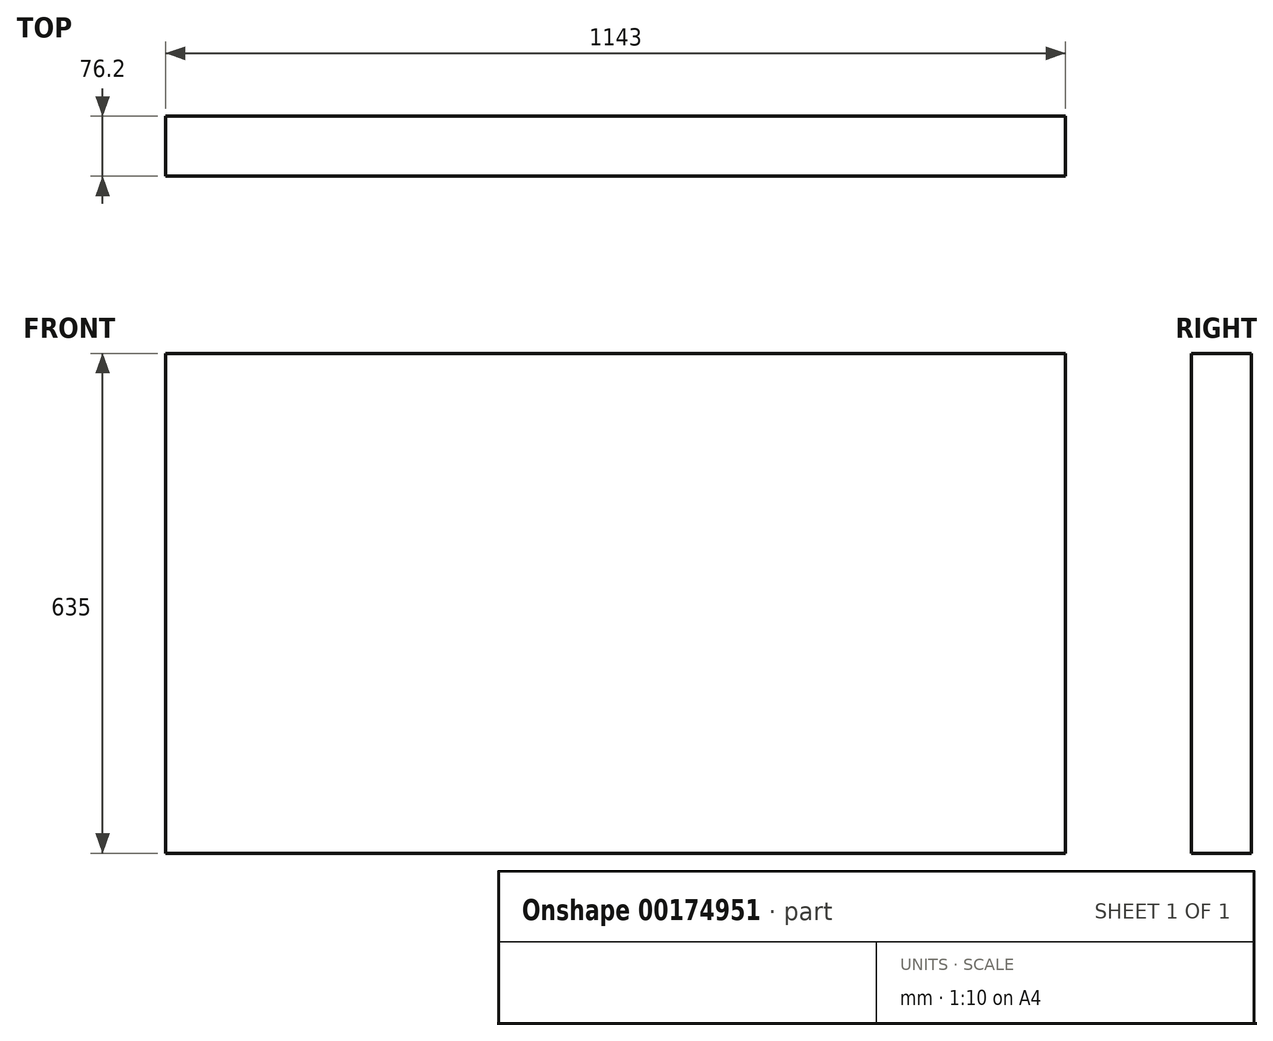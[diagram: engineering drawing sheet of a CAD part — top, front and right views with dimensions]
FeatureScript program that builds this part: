
annotation { "Feature Type Name" : "Feature", "Feature Type Description" : "" }
export const myFeature = defineFeature(function(context is Context, id is Id, definition is map)
    precondition{}
    {
        {
            var Q0;
            Q0=qCreatedBy(makeId("Front.planeOp"),FACE);
            var sketch = newSketch(context, id + "F0", { "sketchPlane" : qUnion([Q0])});
            skLineSegment(sketch, "E0.bottom", {"start": v(571.5, 317.5) * mm, "end": v(-571.5, 317.5) * mm});
            skLineSegment(sketch, "E0.top", {"start": v(571.5, -317.5) * mm, "end": v(-571.5, -317.5) * mm});
            skLineSegment(sketch, "E0.left", {"start": v(571.5, 317.5) * mm, "end": v(571.5, -317.5) * mm});
            skLineSegment(sketch, "E0.right", {"start": v(-571.5, 317.5) * mm, "end": v(-571.5, -317.5) * mm});
            skPoint(sketch, "E0.middle", {"position": v(0, 0) * mm});
            skSolve(sketch);
        }
        {
            var Q0;
            Q0 = qSketchRegion(id + "F0", true);
            extrude(context, id + "F1", {"entities" : qUnion([Q0]), "depth" : 76.2 * mm, "offsetDistance" : 25.4 * mm});
        }
    });
